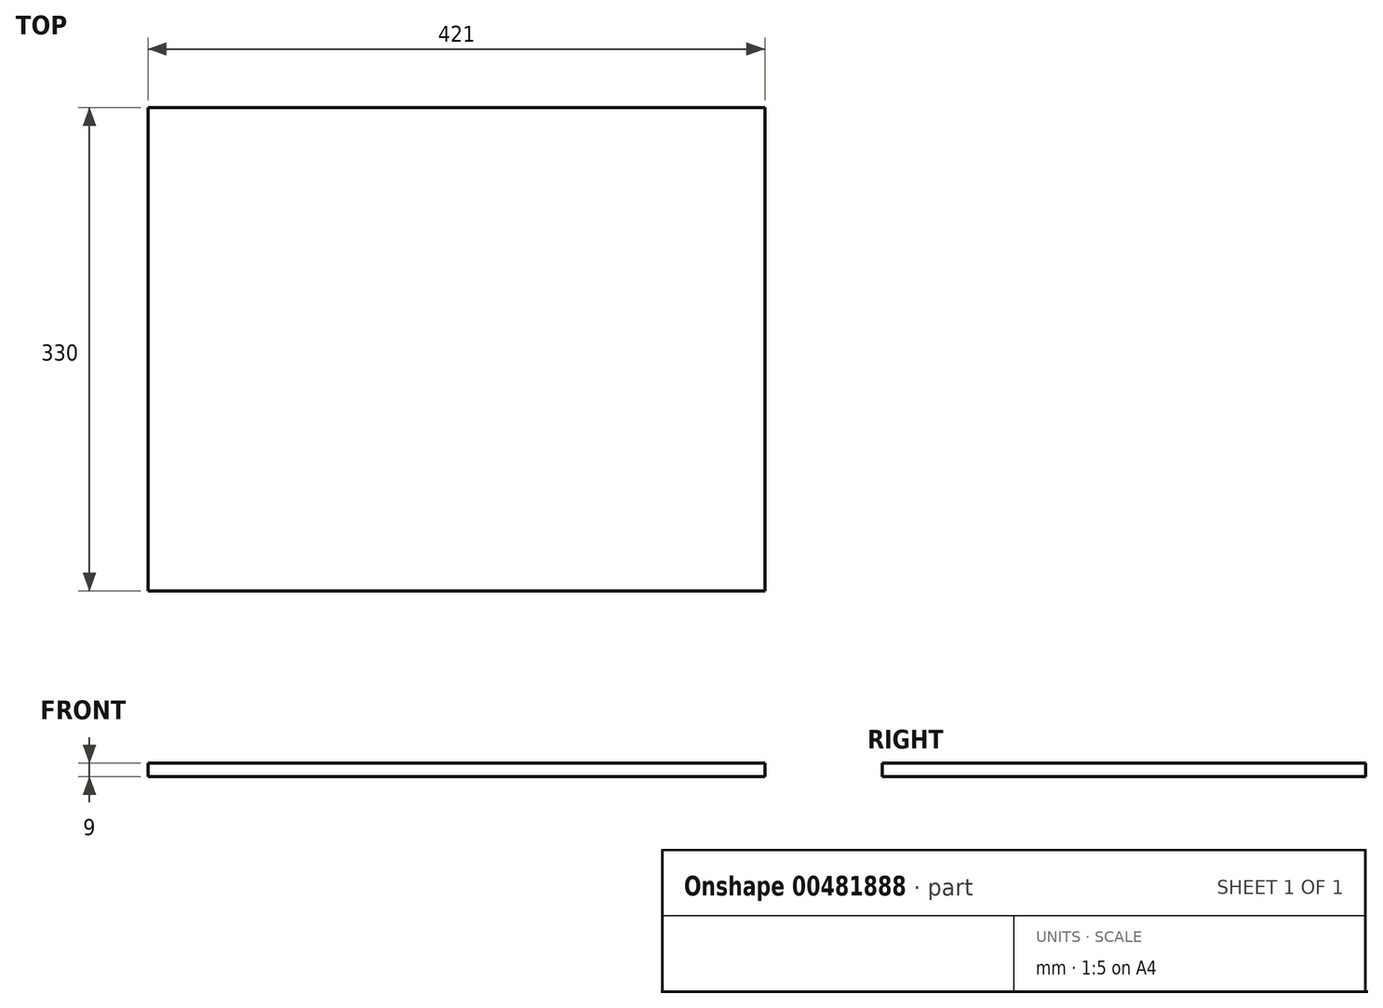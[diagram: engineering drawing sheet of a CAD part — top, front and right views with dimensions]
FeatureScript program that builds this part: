
annotation { "Feature Type Name" : "Feature", "Feature Type Description" : "" }
export const myFeature = defineFeature(function(context is Context, id is Id, definition is map)
    precondition{}
    {
        {
            var Q0;
            Q0=qCreatedBy(makeId("Top.planeOp"),FACE);
            var sketch = newSketch(context, id + "F0", { "sketchPlane" : qUnion([Q0])});
            skLineSegment(sketch, "E0.bottom", {"start": v(0, 0) * mm, "end": v(-421, 0) * mm});
            skLineSegment(sketch, "E0.top", {"start": v(0, 330) * mm, "end": v(-421, 330) * mm});
            skLineSegment(sketch, "E0.right", {"start": v(-421, 0) * mm, "end": v(-421, 330) * mm});
            skLineSegment(sketch, "E1", {"start": v(0, 0) * mm, "end": v(0, 330) * mm});
            skSolve(sketch);
        }
        {
            var Q0;
            Q0 = qSketchRegion(id + "F0", true);
            extrude(context, id + "F1", {"entities" : qUnion([Q0]), "depth" : 9 * mm});
        }
    });
